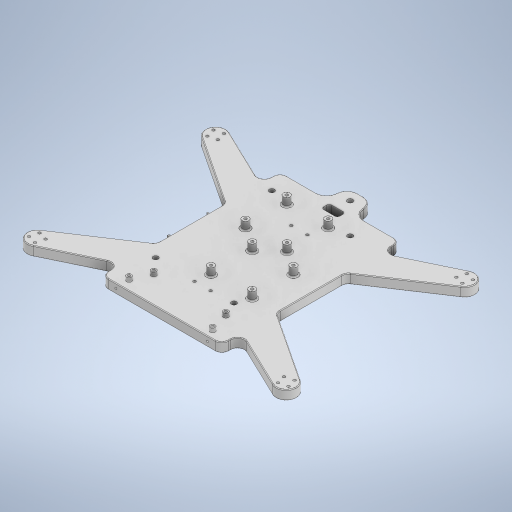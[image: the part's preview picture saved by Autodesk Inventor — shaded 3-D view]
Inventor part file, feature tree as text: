
AUTODESK INVENTOR PART (.ipt)
format: ipt  version: 2023.2 (Build 272271030, 271C)  size: 821,760 bytes
history: native  units: mm
features: extrude x11, sketch x9, projected_geometry x9, fillet x6, plane x1
ambient origin geometry x8: Origin, YZ Plane, XZ Plane, XY Plane, X Axis, Y Axis, Z Axis, Center Point
bodies: Body1 (feature_tree)
feature tree (36):
  sketch  "Sketch1"  dims[d28=39.5mm d29=39.5mm]
  extrude  "Extrusion-kakute"  Depth=39.5mm
  extrude  "Extrusion-intel_d4"  Depth=4.0mm
  extrude  "Extrusion-airframe"  Depth=4.0mm
  fillet  "Fillet-kakute+d4"  Radius=3.75mm
  fillet  "Fillet-gps"  Radius=3.75mm
  fillet  "Fillet-edges_airframe"  Radius=86.0mm
  fillet  "Fillet8"  Radius=58.0mm
  plane  "Work Plane2"
  extrude  "legs_holes"  Depth=4.0mm
  extrude  "intel-realsense-holes"  Depth=50.0mm
  sketch  "Sketch10"  dims[d46=17.0mm d47=4.0mm]
  extrude  "Extrusion10"  Depth=5.0mm TaperAngle=0.0deg
  extrude  "Extrusion11"  Depth=55.0mm
  fillet  "Fillet9"  Radius=9.0mm
  fillet  "Fillet10"  Radius=2.0mm
  extrude  "Extrusion12"  Depth=37.0mm
  sketch  "Sketch12"  dims[d67=5.0mm d77=0.0mm d79=84.5mm]
  extrude  "Extrusion13"  Depth=0.5mm
  extrude  "Extrusion15"  Depth=0.5mm
  extrude  "Extrusion16"  Depth=0.5mm
  sketch  "Sketch4"  dims[d30=100.0mm d36=4.0mm]
  sketch  "Sketch5"  dims[d37=3.75mm d38=4.0mm d39=3.75mm d40=58.0mm d41=3.75mm d42=86.0mm d44=86.0mm d45=58.0mm]
  sketch  "Sketch11"  dims[d48=3.75mm d54=50.0mm]
  sketch  "Sketch13"  dims[d81=15.0mm d84=55.0mm d89=9.0mm d90=2.0mm]
  sketch  "Sketch14"  dims[d91=40.0mm d93=360.0deg d99=37.0mm]
  sketch  "Sketch15"  dims[d100=37.0mm d101=43.0mm d102=44.0mm d103=11.0mm d104=19.0mm d105=5.0mm d106=3.25mm d107=3.25mm d108=20.0mm d109=15.0mm d110=0.0mm d111=10.0mm d112=5.0mm d113=3.25mm d114=3.25mm d115=5.0mm d116=3.25mm d117=3.25mm d118=5.0mm d119=3.25mm d120=3.25mm d121=5.0mm d122=6.25mm d124=6.25mm d125=5.0mm d126=5.0mm d127=5.0mm d128=30.5mm d129=30.5mm d130=30.5mm d131=30.5mm d132=6.25mm d135=3.0mm d157=1.1mm d160=1.7mm d163=7.0mm d167=1.7mm d170=1.0mm d176=89.0mm d177=132.027246mm d178=66.0mm d179=184.262794mm d180=184.262794mm d181=132.0mm d182=7.5mm d183=4.0mm d186=3.0mm d187=45.0deg d188=30.9mm d189=3.0mm d190=3.0mm d191=3.0mm d192=3.0mm d193=20.0mm d195=90.0deg d198=6.0mm d199=6.0mm d200=12.0mm d201=2.0mm d204=13.0mm d205=0.0mm d206=10.0mm d207=0.0mm d208=7.0mm d209=0.0mm d212=1.0mm d214=8.0mm d215=5.0mm d216=0.5mm d218=2.2mm d230=40.0mm d232=20.0mm d233=72.0mm d234=2.2mm d235=16.0mm d237=3.7mm d240=3.7mm d242=3.7mm d243=60.4mm d244=1.7mm d245=6.0mm d246=5.0mm d248=1.7mm d249=66.1mm d250=60.0mm d251=80.0mm d258=22.804mm d259=50.0mm d260=60.0mm d261=80.0mm d262=40.0mm d263=30.0mm d264=2.0mm d265=2.0mm d266=12.0mm d267=4.2mm d268=0.0mm d269=0.0mm d271=1.5mm d272=5.6mm d273=3.0mm d274=1.5mm d275=67.8mm d276=3.0mm d277=5.0mm d278=0.0mm d299=22.804mm d300=2.5mm d301=0.0mm d303=1.0mm d304=135.0deg d305=0.1mm d306=1.0mm d308=3.0mm d309=0.0mm d310=0.1mm d311=0.1mm d312=1.7mm d313=2.5mm d314=2.5mm d315=1.5mm d316=1.0mm d317=15.0mm d318=2.5mm d319=0.0mm d320=1.0mm d321=1.7mm d322=135.0deg d323=2.5mm d324=0.0mm d325=2.0mm d326=2.0mm d327=2.0mm d328=2.0mm d329=2.0mm d330=2.0mm d331=2.0mm d332=2.0mm d335=3.7mm d336=2.0mm d337=2.0mm d338=2.0mm d339=2.0mm d340=2.0mm d341=2.0mm d342=2.0mm d343=2.0mm d344=2.0mm d345=6.0mm d346=0.0mm d347=2.0mm d348=2.0mm d349=2.0mm d350=2.0mm d351=4.0mm d352=0.0mm d68=0.872665mm d69=0.5mm d70=0.872665mm d96=0.5mm d97=0.872665mm d98=0.5mm]
  projected_geometry  "Projected Loop1"
  projected_geometry  "Projected Loop2"
  projected_geometry  "Projected Loop3"
  projected_geometry  "Projected Loop4"
  projected_geometry  "Projected Loop5"
  projected_geometry  "Project Cut Edges1"
  projected_geometry  "Project Cut Edges2"
  projected_geometry  "Project Cut Edges3"
  projected_geometry  "Project Cut Edges4"
